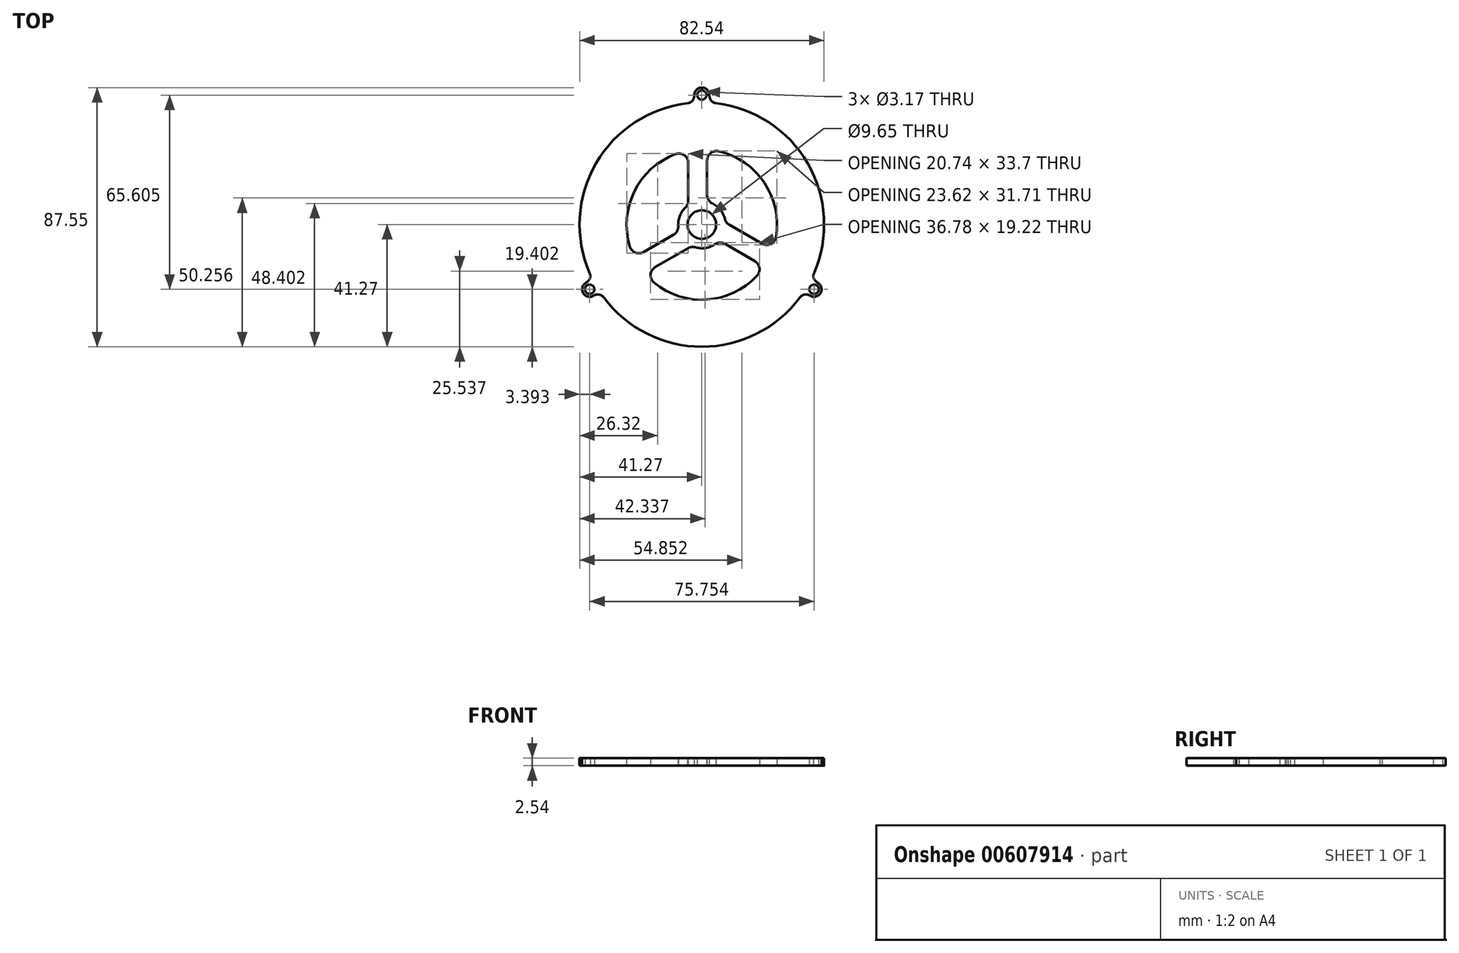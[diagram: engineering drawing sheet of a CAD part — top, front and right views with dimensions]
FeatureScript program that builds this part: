
annotation { "Feature Type Name" : "Feature", "Feature Type Description" : "" }
export const myFeature = defineFeature(function(context is Context, id is Id, definition is map)
    precondition{}
    {
        {
            var Q0;
            Q0=qCreatedBy(makeId("Top.planeOp"),FACE);
            var sketch = newSketch(context, id + "F0", { "sketchPlane" : qUnion([Q0])});
            skCircle(sketch, "E0", {"center": v(0, 0) * mm, "radius": 41.28 * mm});
            skLineSegment(sketch, "E1", {"start": v(-2.54, 41.2) * mm, "end": v(-2.54, 46.28) * mm});
            skLineSegment(sketch, "E2", {"start": v(-2.54, 46.28) * mm, "end": v(2.54, 46.28) * mm});
            skLineSegment(sketch, "E3", {"start": v(2.54, 46.28) * mm, "end": v(2.54, 41.2) * mm});
            skLineSegment(sketch, "E4", {"start": v(-2.54, 46.28) * mm, "end": v(2.54, 41.2) * mm, "construction": true});
            skCircle(sketch, "E5", {"center": v(0, 43.74) * mm, "radius": 1.59 * mm});
            skCircle(sketch, "E6.1.0", {"center": v(-37.88, -21.87) * mm, "radius": 1.59 * mm});
            skLineSegment(sketch, "E6.1.1", {"start": v(-38.8, -25.34) * mm, "end": v(-41.35, -20.94) * mm});
            skLineSegment(sketch, "E6.1.2", {"start": v(-41.35, -20.94) * mm, "end": v(-36.95, -18.4) * mm});
            skLineSegment(sketch, "E6.1.3", {"start": v(-34.4, -22.8) * mm, "end": v(-38.8, -25.34) * mm});
            skCircle(sketch, "E6.2.0", {"center": v(37.88, -21.87) * mm, "radius": 1.59 * mm});
            skLineSegment(sketch, "E6.2.1", {"start": v(41.35, -20.94) * mm, "end": v(38.8, -25.34) * mm});
            skLineSegment(sketch, "E6.2.2", {"start": v(38.8, -25.34) * mm, "end": v(34.4, -22.8) * mm});
            skLineSegment(sketch, "E6.2.3", {"start": v(36.95, -18.4) * mm, "end": v(41.35, -20.94) * mm});
            skCircle(sketch, "E7", {"center": v(0, 0) * mm, "radius": 4.83 * mm});
            skArc(sketch, "E8", {"start": v(-8.86, 23.8) * mm, "mid": v(-22.79, 11.22) * mm, "end": v(-24.27, -7.49) * mm});
            skArc(sketch, "E9", {"start": v(-5.55, 5.76) * mm, "mid": v(-7.46, 2.89) * mm, "end": v(-7.98, -0.52) * mm});
            skLineSegment(sketch, "E10", {"start": v(-4.58, 20.83) * mm, "end": v(-4.58, 8.05) * mm});
            skLineSegment(sketch, "E11", {"start": v(1.77, 21.67) * mm, "end": v(1.77, 10.02) * mm});
            skLineSegment(sketch, "E12.1.0", {"start": v(-19.65, -9.3) * mm, "end": v(-9.56, -3.48) * mm});
            skLineSegment(sketch, "E12.1.1", {"start": v(-15.75, -14.38) * mm, "end": v(-4.68, -8) * mm});
            skLineSegment(sketch, "E12.2.0", {"start": v(17.88, -12.37) * mm, "end": v(7.8, -6.54) * mm});
            skLineSegment(sketch, "E12.2.1", {"start": v(20.33, -6.45) * mm, "end": v(9.26, -0.06) * mm});
            skArc(sketch, "E13.trimOffspring", {"start": v(-2.21, -7.69) * mm, "mid": v(1.23, -7.9) * mm, "end": v(4.44, -6.65) * mm});
            skArc(sketch, "E14.trimOffspring", {"start": v(-16.18, -19.58) * mm, "mid": v(1.68, -25.34) * mm, "end": v(18.62, -17.28) * mm});
            skArc(sketch, "E15.trimOffspring", {"start": v(7.77, 1.93) * mm, "mid": v(6.23, 5.02) * mm, "end": v(3.54, 7.18) * mm});
            skArc(sketch, "E16.trimOffspring", {"start": v(25.05, -4.23) * mm, "mid": v(21.11, 14.12) * mm, "end": v(5.65, 24.76) * mm});
            skPoint(sketch, "E17.visualSharp", {"position": v(-4.58, 24.98) * mm});
            skArc(sketch, "E17.filletArc", {"start": v(-4.58, 20.83) * mm, "mid": v(-5.94, 23.44) * mm, "end": v(-8.86, 23.8) * mm});
            skPoint(sketch, "E18.visualSharp", {"position": v(-4.58, 6.56) * mm});
            skArc(sketch, "E18.filletArc", {"start": v(-5.55, 5.76) * mm, "mid": v(-4.83, 6.8) * mm, "end": v(-4.58, 8.05) * mm});
            skPoint(sketch, "E19.visualSharp", {"position": v(1.77, 7.8) * mm});
            skArc(sketch, "E19.filletArc", {"start": v(1.77, 10.02) * mm, "mid": v(2.25, 8.35) * mm, "end": v(3.54, 7.18) * mm});
            skPoint(sketch, "E20.visualSharp", {"position": v(1.77, 25.34) * mm});
            skArc(sketch, "E20.filletArc", {"start": v(5.65, 24.76) * mm, "mid": v(2.97, 24.15) * mm, "end": v(1.77, 21.67) * mm});
            skPoint(sketch, "E21.visualSharp", {"position": v(-7.64, -2.37) * mm});
            skArc(sketch, "E21.filletArc", {"start": v(-9.56, -3.48) * mm, "mid": v(-8.35, -2.23) * mm, "end": v(-7.98, -0.52) * mm});
            skPoint(sketch, "E22.visualSharp", {"position": v(-22.83, -11.14) * mm});
            skArc(sketch, "E22.filletArc", {"start": v(-24.27, -7.49) * mm, "mid": v(-22.4, -9.5) * mm, "end": v(-19.65, -9.3) * mm});
            skPoint(sketch, "E23.visualSharp", {"position": v(-3.4, -7.25) * mm});
            skArc(sketch, "E23.filletArc", {"start": v(-2.21, -7.69) * mm, "mid": v(-3.48, -7.59) * mm, "end": v(-4.68, -8) * mm});
            skPoint(sketch, "E24.visualSharp", {"position": v(5.87, -5.43) * mm});
            skArc(sketch, "E24.filletArc", {"start": v(7.8, -6.54) * mm, "mid": v(6.1, -6.12) * mm, "end": v(4.44, -6.65) * mm});
            skPoint(sketch, "E25.visualSharp", {"position": v(7.97, 0.69) * mm});
            skArc(sketch, "E25.filletArc", {"start": v(7.77, 1.93) * mm, "mid": v(8.31, 0.78) * mm, "end": v(9.26, -0.06) * mm});
            skPoint(sketch, "E26.visualSharp", {"position": v(23.93, -8.53) * mm});
            skArc(sketch, "E26.filletArc", {"start": v(20.33, -6.45) * mm, "mid": v(23.27, -6.57) * mm, "end": v(25.05, -4.23) * mm});
            skPoint(sketch, "E27.visualSharp", {"position": v(-19.35, -16.46) * mm});
            skArc(sketch, "E27.filletArc", {"start": v(-15.75, -14.38) * mm, "mid": v(-17.32, -16.86) * mm, "end": v(-16.18, -19.58) * mm});
            skPoint(sketch, "E28.visualSharp", {"position": v(21.06, -14.2) * mm});
            skArc(sketch, "E28.filletArc", {"start": v(18.62, -17.28) * mm, "mid": v(19.43, -14.64) * mm, "end": v(17.88, -12.37) * mm});
            skSolve(sketch);
        }
        {
            var Q0;
            {var subQ0=sQuery(id+"F0.wireOp",EDGE,"E0");var subQ4=makeQuery(id+"F0.imprint","INTERSECT",VERTEX,{"derivedFrom":[subQ0,sQuery(id+"F0.wireOp",EDGE,"E1")]});Q0=makeQuery(id+"F0.imprint","IMPRINT",FACE,{"disambiguationData":[TD([[makeQuery(id+"F0.imprint","IMPRINT",EDGE,{"disambiguationData":[TD([[subQ4,1.0]])],"derivedFrom":subQ0}),1.0]])]});}
            var Q1;
            {var subQ1=sQuery(id+"F0.wireOp",EDGE,"E1");Q1=makeQuery(id+"F0.imprint","IMPRINT",FACE,{"disambiguationData":[TD([[makeQuery(id+"F0.imprint","IMPRINT",EDGE,{"derivedFrom":subQ1}),-1.0]])]});}
            var Q2;
            Q2=makeQuery(id+"F0.imprint","IMPRINT",FACE,{"disambiguationData":[TD([[makeQuery(id+"F0.imprint","IMPRINT",EDGE,{"derivedFrom":sQuery(id+"F0.wireOp",EDGE,"E6.1.0")}),-1.0]])]});
            var Q3;
            Q3=makeQuery(id+"F0.imprint","IMPRINT",FACE,{"disambiguationData":[TD([[makeQuery(id+"F0.imprint","IMPRINT",EDGE,{"derivedFrom":sQuery(id+"F0.wireOp",EDGE,"E6.2.0")}),-1.0]])]});
            extrude(context, id + "F1", {"entities" : qUnion([Q0, Q1, Q2, Q3]), "depth" : 2.54 * mm, "offsetDistance" : 25.4 * mm});
        }
        {
            var Q0;
            Q0=makeQuery(id+"F1.opExtrude","SWEPT_EDGE",EDGE,{"disambiguationData":[OSD([sQuery(id+"F0.wireOp",EDGE,"E0"),sQuery(id+"F0.wireOp",EDGE,"E6.1.3")])]});
            var Q1;
            Q1=makeQuery(id+"F1.opExtrude","SWEPT_EDGE",EDGE,{"disambiguationData":[OSD([sQuery(id+"F0.wireOp",EDGE,"E6.1.1"),sQuery(id+"F0.wireOp",EDGE,"E6.1.3")])]});
            var Q2;
            Q2=makeQuery(id+"F1.opExtrude","SWEPT_EDGE",EDGE,{"disambiguationData":[OSD([sQuery(id+"F0.wireOp",EDGE,"E6.1.1"),sQuery(id+"F0.wireOp",EDGE,"E6.1.2")])]});
            var Q3;
            Q3=makeQuery(id+"F1.opExtrude","SWEPT_EDGE",EDGE,{"disambiguationData":[OSD([sQuery(id+"F0.wireOp",EDGE,"E0"),sQuery(id+"F0.wireOp",EDGE,"E6.1.2")])]});
            var Q4;
            Q4=makeQuery(id+"F1.opExtrude","SWEPT_EDGE",EDGE,{"disambiguationData":[OSD([sQuery(id+"F0.wireOp",EDGE,"E0"),sQuery(id+"F0.wireOp",EDGE,"E6.2.2")])]});
            var Q5;
            Q5=makeQuery(id+"F1.opExtrude","SWEPT_EDGE",EDGE,{"disambiguationData":[OSD([sQuery(id+"F0.wireOp",EDGE,"E6.2.1"),sQuery(id+"F0.wireOp",EDGE,"E6.2.2")])]});
            var Q6;
            Q6=makeQuery(id+"F1.opExtrude","SWEPT_EDGE",EDGE,{"disambiguationData":[OSD([sQuery(id+"F0.wireOp",EDGE,"E6.2.1"),sQuery(id+"F0.wireOp",EDGE,"E6.2.3")])]});
            var Q7;
            Q7=makeQuery(id+"F1.opExtrude","SWEPT_EDGE",EDGE,{"disambiguationData":[OSD([sQuery(id+"F0.wireOp",EDGE,"E0"),sQuery(id+"F0.wireOp",EDGE,"E6.2.3")])]});
            var Q8;
            Q8=makeQuery(id+"F1.opExtrude","SWEPT_EDGE",EDGE,{"disambiguationData":[OSD([sQuery(id+"F0.wireOp",EDGE,"E0"),sQuery(id+"F0.wireOp",EDGE,"E3")])]});
            var Q9;
            Q9=makeQuery(id+"F1.opExtrude","SWEPT_EDGE",EDGE,{"disambiguationData":[OSD([sQuery(id+"F0.wireOp",EDGE,"E2"),sQuery(id+"F0.wireOp",EDGE,"E3")])]});
            var Q10;
            Q10=makeQuery(id+"F1.opExtrude","SWEPT_EDGE",EDGE,{"disambiguationData":[OSD([sQuery(id+"F0.wireOp",EDGE,"E0"),sQuery(id+"F0.wireOp",EDGE,"E1")])]});
            var Q11;
            Q11=makeQuery(id+"F1.opExtrude","SWEPT_EDGE",EDGE,{"disambiguationData":[OSD([sQuery(id+"F0.wireOp",EDGE,"E1"),sQuery(id+"F0.wireOp",EDGE,"E2")])]});
            fillet(context, id + "F2", {"entities" : qUnion([Q0, Q1, Q2, Q3, Q4, Q5, Q6, Q7, Q8, Q9, Q10, Q11]), "radius" : 2.54 * mm, "tangentPropagation" : true, "allowEdgeOverflow" : false});
        }
    });
